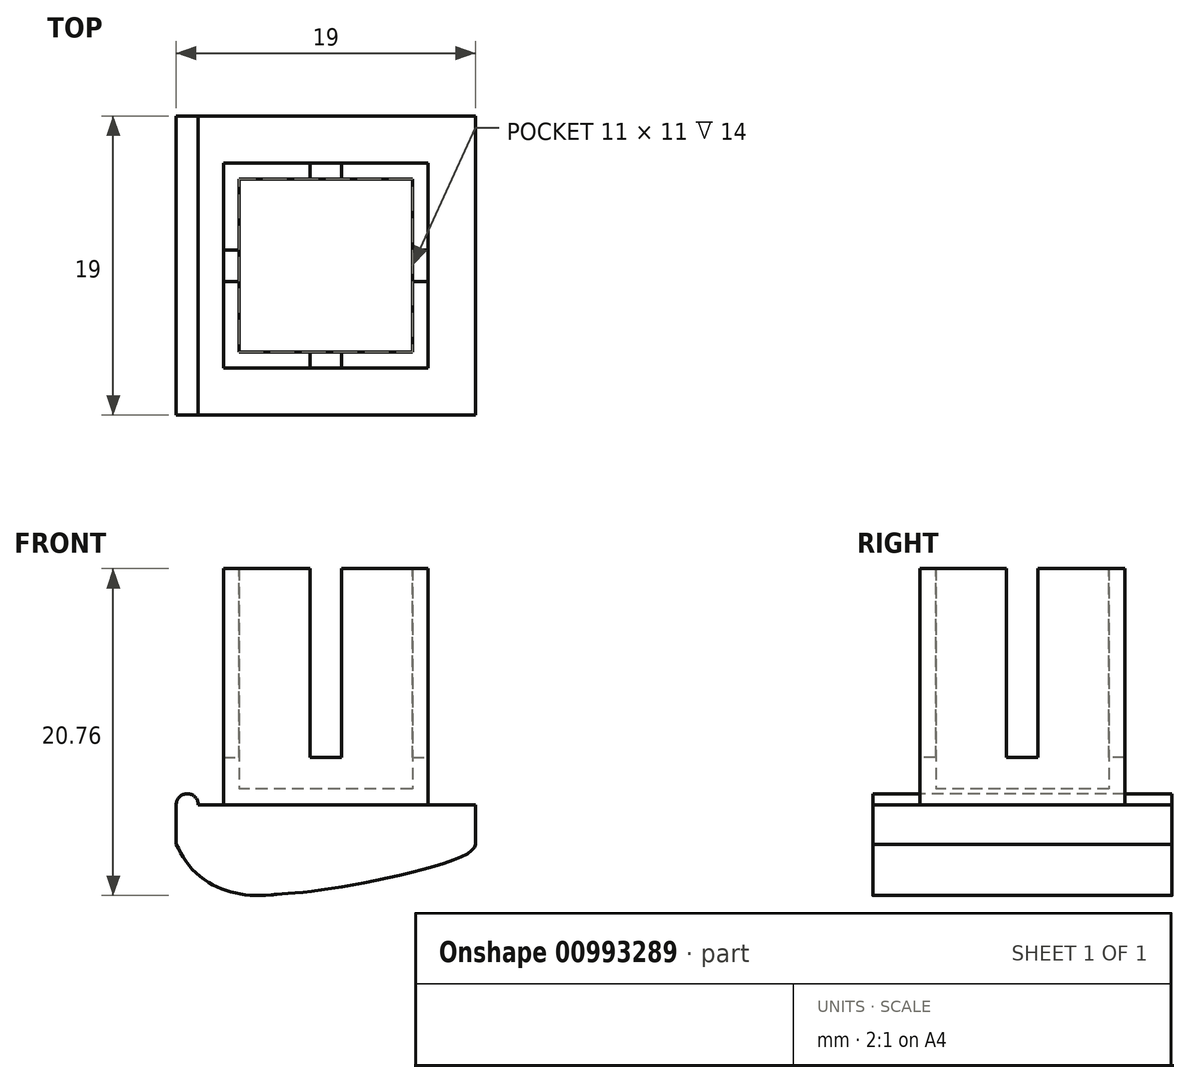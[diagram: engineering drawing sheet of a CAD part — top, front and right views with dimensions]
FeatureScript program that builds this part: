
annotation { "Feature Type Name" : "Feature", "Feature Type Description" : "" }
export const myFeature = defineFeature(function(context is Context, id is Id, definition is map)
    precondition{}
    {
        {
            var Q0;
            Q0=qCreatedBy(makeId("Top.planeOp"),FACE);
            var sketch = newSketch(context, id + "F0", { "sketchPlane" : qUnion([Q0])});
            skLineSegment(sketch, "E0", {"start": v(0, 0) * mm, "end": v(0, 6.5) * mm, "construction": true});
            skLineSegment(sketch, "E1", {"start": v(0, 6.5) * mm, "end": v(6.5, 6.5) * mm, "construction": true});
            skLineSegment(sketch, "E2.bottom", {"start": v(6.5, 6.5) * mm, "end": v(-6.5, 6.5) * mm});
            skLineSegment(sketch, "E2.top", {"start": v(6.5, -6.5) * mm, "end": v(-6.5, -6.5) * mm});
            skLineSegment(sketch, "E2.left", {"start": v(6.5, 6.5) * mm, "end": v(6.5, -6.5) * mm});
            skLineSegment(sketch, "E2.right", {"start": v(-6.5, 6.5) * mm, "end": v(-6.5, -6.5) * mm});
            skLineSegment(sketch, "E3.bottom", {"start": v(1, 6.5) * mm, "end": v(-1, 6.5) * mm});
            skLineSegment(sketch, "E3.top", {"start": v(1, -6.5) * mm, "end": v(-1, -6.5) * mm});
            skLineSegment(sketch, "E3.left", {"start": v(1, 6.5) * mm, "end": v(1, -6.5) * mm});
            skLineSegment(sketch, "E3.right", {"start": v(-1, 6.5) * mm, "end": v(-1, -6.5) * mm});
            skLineSegment(sketch, "E4.bottom", {"start": v(-6.5, 1) * mm, "end": v(6.5, 1) * mm});
            skLineSegment(sketch, "E4.top", {"start": v(-6.5, -1) * mm, "end": v(6.5, -1) * mm});
            skLineSegment(sketch, "E4.left", {"start": v(-6.5, 1) * mm, "end": v(-6.5, -1) * mm});
            skLineSegment(sketch, "E4.right", {"start": v(6.5, 1) * mm, "end": v(6.5, -1) * mm});
            skSolve(sketch);
        }
        {
            var Q0;
            {var subQ0=sQuery(id+"F0.wireOp",EDGE,"E2.left");var subQ1=sQuery(id+"F0.wireOp",EDGE,"E2.bottom");var subQ2=makeQuery(id+"F0.imprint","INTERSECT",VERTEX,{"derivedFrom":[subQ1,subQ0]});Q0=makeQuery(id+"F0.imprint","IMPRINT",FACE,{"disambiguationData":[TD([[makeQuery(id+"F0.imprint","IMPRINT",EDGE,{"disambiguationData":[TD([[subQ2,-1.0]])],"derivedFrom":subQ1}),1.0]])]});}
            var Q1;
            {var subQ0=sQuery(id+"F0.wireOp",EDGE,"E3.right");var subQ1=sQuery(id+"F0.wireOp",EDGE,"E2.bottom");var subQ2=makeQuery(id+"F0.imprint","INTERSECT",VERTEX,{"derivedFrom":[subQ1,subQ0]});Q1=makeQuery(id+"F0.imprint","IMPRINT",FACE,{"disambiguationData":[TD([[makeQuery(id+"F0.imprint","IMPRINT",EDGE,{"disambiguationData":[TD([[subQ2,1.0]])],"derivedFrom":subQ1}),1.0]])]});}
            var Q2;
            {var subQ0=sQuery(id+"F0.wireOp",EDGE,"E3.right");var subQ1=sQuery(id+"F0.wireOp",EDGE,"E2.bottom");var subQ2=makeQuery(id+"F0.imprint","INTERSECT",VERTEX,{"derivedFrom":[subQ1,subQ0]});Q2=makeQuery(id+"F0.imprint","IMPRINT",FACE,{"disambiguationData":[TD([[makeQuery(id+"F0.imprint","IMPRINT",EDGE,{"disambiguationData":[TD([[subQ2,-1.0]])],"derivedFrom":subQ1}),1.0]])]});}
            var Q3;
            {var subQ0=sQuery(id+"F0.wireOp",EDGE,"E4.top");var subQ1=sQuery(id+"F0.wireOp",EDGE,"E2.right");var subQ2=makeQuery(id+"F0.imprint","INTERSECT",VERTEX,{"derivedFrom":[subQ1,subQ0]});Q3=makeQuery(id+"F0.imprint","IMPRINT",FACE,{"disambiguationData":[TD([[makeQuery(id+"F0.imprint","IMPRINT",EDGE,{"disambiguationData":[TD([[subQ2,1.0]])],"derivedFrom":subQ1}),1.0]])]});}
            var Q4;
            {var subQ0=sQuery(id+"F0.wireOp",EDGE,"E4.top");var subQ1=sQuery(id+"F0.wireOp",EDGE,"E3.left");var subQ2=makeQuery(id+"F0.imprint","INTERSECT",VERTEX,{"derivedFrom":[subQ1,subQ0]});Q4=makeQuery(id+"F0.imprint","IMPRINT",FACE,{"disambiguationData":[TD([[makeQuery(id+"F0.imprint","IMPRINT",EDGE,{"disambiguationData":[TD([[subQ2,1.0]])],"derivedFrom":subQ1}),-1.0]])]});}
            var Q5;
            {var subQ0=sQuery(id+"F0.wireOp",EDGE,"E4.top");var subQ1=sQuery(id+"F0.wireOp",EDGE,"E2.left");var subQ2=makeQuery(id+"F0.imprint","INTERSECT",VERTEX,{"derivedFrom":[subQ1,subQ0]});Q5=makeQuery(id+"F0.imprint","IMPRINT",FACE,{"disambiguationData":[TD([[makeQuery(id+"F0.imprint","IMPRINT",EDGE,{"disambiguationData":[TD([[subQ2,1.0]])],"derivedFrom":subQ1}),-1.0]])]});}
            var Q6;
            {var subQ0=sQuery(id+"F0.wireOp",EDGE,"E2.left");var subQ1=sQuery(id+"F0.wireOp",EDGE,"E2.top");var subQ2=makeQuery(id+"F0.imprint","INTERSECT",VERTEX,{"derivedFrom":[subQ1,subQ0]});Q6=makeQuery(id+"F0.imprint","IMPRINT",FACE,{"disambiguationData":[TD([[makeQuery(id+"F0.imprint","IMPRINT",EDGE,{"disambiguationData":[TD([[subQ2,-1.0]])],"derivedFrom":subQ1}),-1.0]])]});}
            var Q7;
            {var subQ0=sQuery(id+"F0.wireOp",EDGE,"E3.right");var subQ1=sQuery(id+"F0.wireOp",EDGE,"E2.top");var subQ2=makeQuery(id+"F0.imprint","INTERSECT",VERTEX,{"derivedFrom":[subQ1,subQ0]});Q7=makeQuery(id+"F0.imprint","IMPRINT",FACE,{"disambiguationData":[TD([[makeQuery(id+"F0.imprint","IMPRINT",EDGE,{"disambiguationData":[TD([[subQ2,1.0]])],"derivedFrom":subQ1}),-1.0]])]});}
            var Q8;
            {var subQ0=sQuery(id+"F0.wireOp",EDGE,"E3.right");var subQ1=sQuery(id+"F0.wireOp",EDGE,"E2.top");var subQ2=makeQuery(id+"F0.imprint","INTERSECT",VERTEX,{"derivedFrom":[subQ1,subQ0]});Q8=makeQuery(id+"F0.imprint","IMPRINT",FACE,{"disambiguationData":[TD([[makeQuery(id+"F0.imprint","IMPRINT",EDGE,{"disambiguationData":[TD([[subQ2,-1.0]])],"derivedFrom":subQ1}),-1.0]])]});}
            extrude(context, id + "F1", {"entities" : qUnion([Q0, Q1, Q2, Q3, Q4, Q5, Q6, Q7, Q8]), "depth" : 15 * mm, "offsetDistance" : 25 * mm});
        }
        {
            var Q0;
            Q0=makeQuery(id+"F1.opExtrude","CAP_FACE",FACE,{"disambiguationData":[OSD([sQuery(id+"F0.wireOp",EDGE,"E2.bottom"),sQuery(id+"F0.wireOp",EDGE,"E2.top"),sQuery(id+"F0.wireOp",EDGE,"E2.left"),sQuery(id+"F0.wireOp",EDGE,"E2.right")])],"isStart":false});
            shell(context, id + "F2", {"entities" : qUnion([Q0]), "thickness" : 1 * mm});
        }
        {
            var Q0;
            {var subQ0=sQuery(id+"F0.wireOp",EDGE,"E4.top");var subQ1=sQuery(id+"F0.wireOp",EDGE,"E2.right");var subQ2=makeQuery(id+"F0.imprint","INTERSECT",VERTEX,{"derivedFrom":[subQ1,subQ0]});Q0=makeQuery(id+"F0.imprint","IMPRINT",FACE,{"disambiguationData":[TD([[makeQuery(id+"F0.imprint","IMPRINT",EDGE,{"disambiguationData":[TD([[subQ2,1.0]])],"derivedFrom":subQ1}),1.0]])]});}
            var Q1;
            {var subQ0=sQuery(id+"F0.wireOp",EDGE,"E3.right");var subQ1=sQuery(id+"F0.wireOp",EDGE,"E2.bottom");var subQ2=makeQuery(id+"F0.imprint","INTERSECT",VERTEX,{"derivedFrom":[subQ1,subQ0]});Q1=makeQuery(id+"F0.imprint","IMPRINT",FACE,{"disambiguationData":[TD([[makeQuery(id+"F0.imprint","IMPRINT",EDGE,{"disambiguationData":[TD([[subQ2,1.0]])],"derivedFrom":subQ1}),1.0]])]});}
            var Q2;
            {var subQ0=sQuery(id+"F0.wireOp",EDGE,"E4.top");var subQ1=sQuery(id+"F0.wireOp",EDGE,"E2.left");var subQ2=makeQuery(id+"F0.imprint","INTERSECT",VERTEX,{"derivedFrom":[subQ1,subQ0]});Q2=makeQuery(id+"F0.imprint","IMPRINT",FACE,{"disambiguationData":[TD([[makeQuery(id+"F0.imprint","IMPRINT",EDGE,{"disambiguationData":[TD([[subQ2,1.0]])],"derivedFrom":subQ1}),-1.0]])]});}
            var Q3;
            {var subQ0=sQuery(id+"F0.wireOp",EDGE,"E3.right");var subQ1=sQuery(id+"F0.wireOp",EDGE,"E2.top");var subQ2=makeQuery(id+"F0.imprint","INTERSECT",VERTEX,{"derivedFrom":[subQ1,subQ0]});Q3=makeQuery(id+"F0.imprint","IMPRINT",FACE,{"disambiguationData":[TD([[makeQuery(id+"F0.imprint","IMPRINT",EDGE,{"disambiguationData":[TD([[subQ2,1.0]])],"derivedFrom":subQ1}),-1.0]])]});}
            extrude(context, id + "F3", {"entities" : qUnion([Q0, Q1, Q2, Q3]), "operationType" : NewBodyOperationType.REMOVE, "depth" : 25 * mm, "offsetDistance" : 25 * mm, "hasSecondDirection" : true, "secondDirectionOppositeDirection" : true, "secondDirectionDepth" : -3 * mm});
        }
        {
            var Q0;
            Q0=makeQuery(id+"F1.opExtrude","SWEPT_FACE",FACE,{"disambiguationData":[OSD([sQuery(id+"F0.wireOp",EDGE,"E2.top")])]});
            var sketch = newSketch(context, id + "F4", { "sketchPlane" : qUnion([Q0])});
            skLineSegment(sketch, "E5.bottom", {"start": v(9.5, 0) * mm, "end": v(-9.5, 0) * mm});
            skLineSegment(sketch, "E5.top", {"start": v(9.5, -2.5) * mm, "end": v(-9.5, -2.5) * mm});
            skLineSegment(sketch, "E5.left", {"start": v(9.5, 0) * mm, "end": v(9.5, -2.5) * mm});
            skLineSegment(sketch, "E5.right", {"start": v(-9.5, 0) * mm, "end": v(-9.5, -2.5) * mm});
            skArc(sketch, "E6", {"start": v(-9.5, -2.5) * mm, "mid": v(-4.75, -5.7) * mm, "end": v(0, -2.5) * mm, "construction": true});
            skPoint(sketch, "E7.1.internal.snap0", {"position": v(-4.75, -5.7) * mm});
            skFitSpline(sketch, "E7", {"points": [v(-4.75, -5.7) * mm, v(-3.09, -5.7) * mm, v(-0.94, -5.5) * mm, v(4.54, -4.52) * mm, v(9.02, -3.1) * mm, v(9.5, -2.5) * mm], "startDerivative": vector(23.09, -1.04) * mm, "endDerivative": vector(0.55, 6.07) * mm});
            skFitSpline(sketch, "E8", {"points": [v(-3.09, -5.7) * mm, v(-4.75, -5.74) * mm, v(-6.21, -5.48) * mm, v(-7.54, -4.87) * mm, v(-8.75, -3.78) * mm, v(-9.5, -2.5) * mm], "startDerivative": vector(-8.13, -0.63) * mm, "endDerivative": vector(-3.39, 6.68) * mm});
            skArc(sketch, "E9", {"start": v(-8.1, 0) * mm, "mid": v(-8.8, 0.7) * mm, "end": v(-9.5, 0) * mm});
            skArc(sketch, "E10.MirrorCS", {"start": v(8.1, 0) * mm, "mid": v(8.8, 0.7) * mm, "end": v(9.5, 0) * mm});
            skSolve(sketch);
        }
        {
            var Q0;
            Q0=makeQuery(id+"F4.imprint","IMPRINT",FACE,{"disambiguationData":[TD([[makeQuery(id+"F4.imprint","IMPRINT",EDGE,{"derivedFrom":sQuery(id+"F4.wireOp",EDGE,"E5.top")}),-1.0]])]});
            var Q1;
            {var subQ0=sQuery(id+"F4.wireOp",EDGE,"E9");Q1=makeQuery(id+"F4.imprint","IMPRINT",FACE,{"disambiguationData":[TD([[makeQuery(id+"F4.imprint","IMPRINT",EDGE,{"derivedFrom":subQ0}),1.0]])]});}
            var Q2;
            {var subQ0=sQuery(id+"F4.wireOp",EDGE,"E10.MirrorCS");Q2=makeQuery(id+"F4.imprint","IMPRINT",FACE,{"disambiguationData":[TD([[makeQuery(id+"F4.imprint","IMPRINT",EDGE,{"derivedFrom":subQ0}),-1.0]])]});}
            var Q3;
            {var subQ0=sQuery(id+"F4.wireOp",EDGE,"E5.top");Q3=makeQuery(id+"F4.imprint","IMPRINT",FACE,{"disambiguationData":[TD([[makeQuery(id+"F4.imprint","IMPRINT",EDGE,{"derivedFrom":subQ0}),1.0]])]});}
            extrude(context, id + "F5", {"entities" : qUnion([Q0, Q1, Q2, Q3]), "operationType" : NewBodyOperationType.ADD, "oppositeDirection" : true, "depth" : 16 * mm, "offsetDistance" : 25 * mm, "hasSecondDirection" : true, "secondDirectionOppositeDirection" : false, "secondDirectionDepth" : 3 * mm});
        }
    });
